# Revit family: P191568KX-059c_KICU509X
name_source: partatom
category: Specialty Equipment
units: mm (PartAtom-declared; Revit-internal decimal feet)

## family parameters
Always vertical = Yes
Cut with Voids When Loaded = No
Enable Cutting in Views = No
Maintain Annotation Orientation = No
Part Type = Normal
Room Calculation Point = No
Round Connector Dimension = Use Diameter
Shared = No
Work Plane-Based = No

## types (2) — shared parameters
Amps = 40 A
Body Material = ARCAT - Metal - Steel - Stainless
Cooktop Material = ARCAT - Glass - Black
Default Elevation = 0"
Depth = 21 5/16"
Description = 30-Inch 4 Element Induction Cooktop, Architect® Series II
Table de cuisson à induction de 30 po KitchenAid®, 4 éléments, série Architect® II
Dimension Guide = http://access.whirlpool.com Guide&sku=KICU509XBL&language=EN
http://access.whirlpool.com Guide&sku=KICU509XBL&language=EN
Family Name = COOKING
Feature 1 = 4-Element Cooktop
Table de cuisson à 4 éléments
Feature 2 = 2 Elements with Bridge Function
2 éléments avec fonction de liaison
Feature 3 = 12 Heat Level Settings
12 réglages de température
Grid Material = ARCAT - Metal - Steel - Black
Height = 3 1/8"
Installation-Fabrication = https://www.whirlpool.com
http://access.whirlpool.com Instruction&sku=KICU509XBL&language=FR
Knob Material = ARCAT - Metal - Steel - Gray
Manufacturer = KitchenAid
Voltage = 240 V
Width = 30 3/4"

## type names
- KICU509XSS
- KICU509XBL

note: column(s) folded — value = type name in every type: Model
type visibility flags: 2 boolean params named "<type name>" — each type sets only its own to Yes (folded from table)

## geometry (parser evidence)
native form markers: Sweep x4
no freeform markers — native parametric forms only
